# Revit family: DuraCare-Settee-Bench-Covert+++++
name_source: partatom
category: Furniture
units: mm (PartAtom-declared; Revit-internal decimal feet)

## family parameters
Always vertical = Yes
Cut with Voids When Loaded = No
OmniClass Number = 23.40.20.00
OmniClass Title = General Furniture and Specialties
Room Calculation Point = No
Shared = No
Work Plane-Based = No

## types (1)
- BE-974
    Assembly Code = E2020200
    Default Elevation = 0"
    Depth = 20 1/2"
    Description = Settee bench 50"W x 20.5"D x 27"H - aluminum frame - wood grain finish
    Height = 27"
    Keynote = 12500
    Low Emitting Finish = Yes
    Low Emitting Material = Yes
    Manufacturer = DuraCare Seating
    Model = BE-974
    Percentage of Recycled Content = 0
    Product Documentation Link = https://duracareseating.com
    Revit Model Built By = https://servex-us.com
    Salvage or Reuse = Yes
    Seat Height = 18 1/2"
    Type Comments = Covert
    URL = https://duracareseating.com
    Width = 50"

## geometry (parser evidence)
native form markers: Sweep x2
no freeform markers — native parametric forms only
